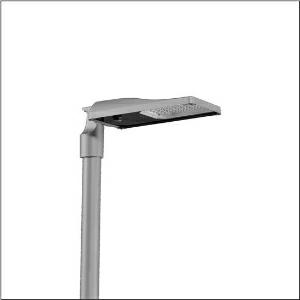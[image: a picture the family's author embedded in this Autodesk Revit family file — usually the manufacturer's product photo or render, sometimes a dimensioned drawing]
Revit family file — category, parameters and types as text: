
# Revit family: streetlight_sl_31_mini___st1_0a_5xh6d3ar08ja_50f1
name_source: partatom
category: Lighting Fixtures
units: mm (PartAtom-declared; Revit-internal decimal feet)

## family parameters
Cut with Voids When Loaded = No
Host = Face
Light Source = No
Part Type = Normal
Room Calculation Point = No
Round Connector Dimension = Use Diameter
Shared = No

## types (1)
- --- (1 x LED, 12270 lm, 82.5 W, 3000K)
    Apparent Load = 83 VA
    CIE Flux Codes = 40 73 97 100 100
    Color Rendering = 70
    Color Temperature = 3000K
    Default Elevation = 1800 mm
    Description = Streetlight SL 31 mini D4i mast luminaire for post-top, side-entry; light control with lens of PMMA; light distribution: ST1.0a, direct asymmetric distribution, for standard-compliant lighting for roads and squares; LED: luminous flux: 12.270lm, light colour: 730, colour temperature: 3000K; luminous efficacy: 148,7lm/W; control: pre-setting: logarithmic dimming characteristic, flexible luminous flux parameterisation, time-dependent luminous flux control, constant luminous flux control, power reduction, intelligent temperature release in ECG and LED module, overheat protection; luminaire housing, of diecast aluminium, Siteco® metallic grey (DB 702S), corrosivity category C5 high according to DIN EN ISO 12944; cover of toughened safety glass, transparent, opened without tools; mast flange of diecast aluminium, Siteco® metallic grey (DB 702S), spigot size: 76/60mm, mast flange included unmounted; with cable H07RN-F 2x 1.5mm², cable length: 10,5m, connection cable pre-assembled; mains connection: 220..240V, AC, 50/60Hz; power consumption (at start of service life): 82,5W / (at end of service life): 90,1W / (with reduced operation 50%): 36,8W; protection rating (complete): IP66; insulation class (complete): insulation class II (safety insulation); impact resistance: IK09; certification: CE, ENEC, ENEC+, VDE, UKCA, ZD4i; permissible operating ambient temperature for outdoor applications: -40..+50°C; packaging unit: 1 piece

Light Distribution: ST1.0a
    Height = 76 mm
    Lamp = 1 x LED
    Lamp Light Flux = 12270 lm
    Lamp Power = 82.5 W
    Lamp count = 1
    Length = 547 mm
    Luminous efficacy = 149 lm/W
    Manufacturer = Siteco
    ModVariant = No
    Model = 5XH6D3AR08JA
    Number of Poles = 1
    OnlyDefault = Yes
    Power Factor = 1
    Product Name = Streetlight SL 31 mini | ST1.0a
    Product group = mast luminaire | pylon top
    ProductGroupID = 6100
    Protection Class = Protection class II
    Protection Degree = IP 66
    RLX_Detail_Level = 1
    RLX_Emergency_Light_Flux = 0 lm
    RLX_Emergency_Type = 0
    RLX_Emergency_Type_DB = No
    RlxData = <blob elided: 39917 chars, md5=94aac52d>
    Socket = socket
    Standby Power = 0 W
    System Light Flux = 12270 lm
    System Power = 83 W
    Type Comments = factory setting: luminous flux: 100 % | dim-lin: 254 | 870 mA
    Type Image = l_1300328.jpg
    URL = http://relux.com
    VarID = @adj_050326
    Voltage = 0 V
    Weight = 0.00 kg
    Width = 265 mm

## geometry (parser evidence)
native form markers: Blend x4, Sweep x9
no freeform markers — native parametric forms only
